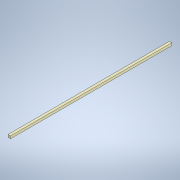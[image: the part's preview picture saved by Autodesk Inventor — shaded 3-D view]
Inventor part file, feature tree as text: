
AUTODESK INVENTOR PART (.ipt)
format: ipt  version: 2020 (Build 240168000, 168)  size: 95,744 bytes
history: native  units: in
note: dims shown in document units (in); Inventor stores cm internally (conversion verified against a paired STEP export)
features: extrude x1, sketch x1
ambient origin geometry x8: Origin, YZ Plane, XZ Plane, XY Plane, X Axis, Y Axis, Z Axis, Center Point
bodies: Solid1 (feature_tree)
feature tree (2):
  extrude  "Extrusion1"  Depth=0.1875in
  sketch  "Sketch1"  dims[d0=0.1875in d1=0.1875in d2=12.0in d3=0.0in]
